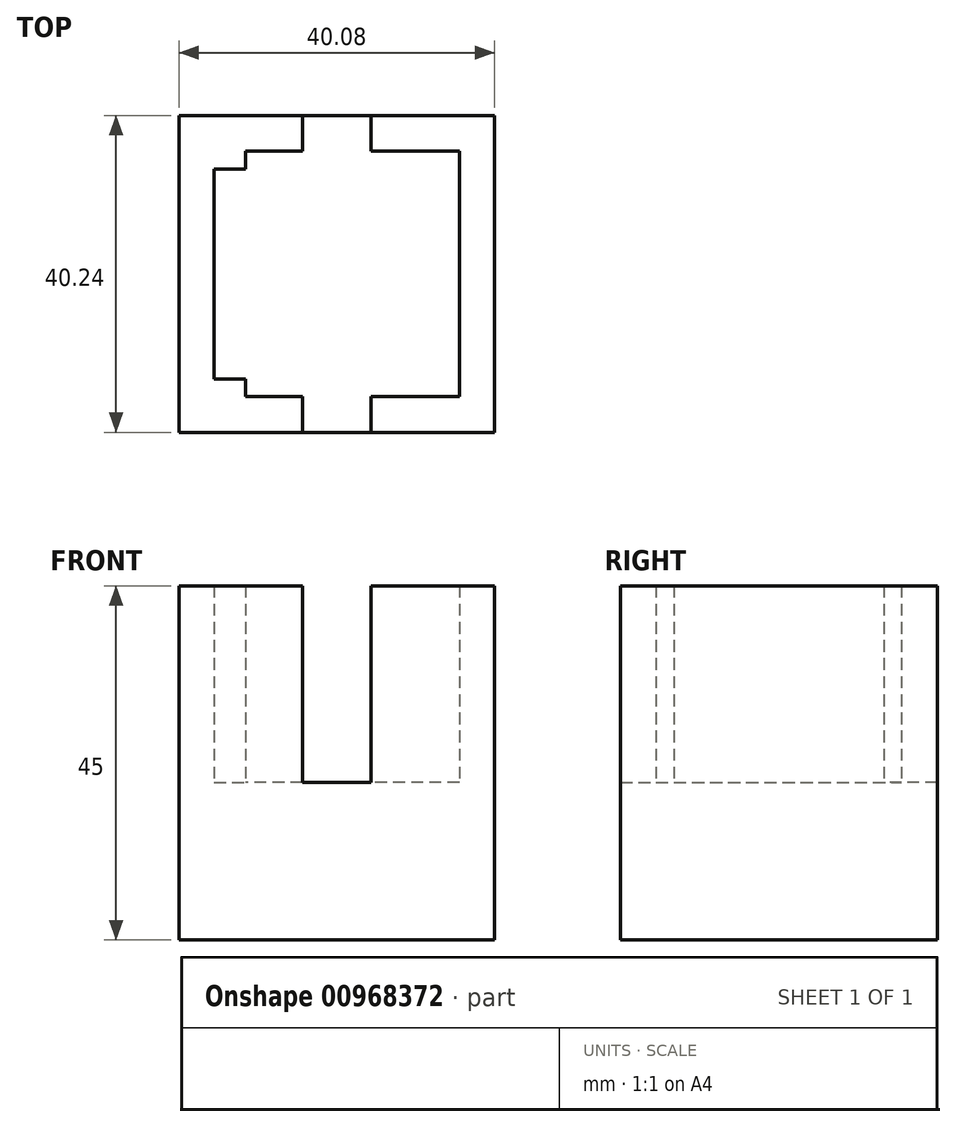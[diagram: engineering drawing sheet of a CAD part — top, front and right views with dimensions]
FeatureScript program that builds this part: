
annotation { "Feature Type Name" : "Feature", "Feature Type Description" : "" }
export const myFeature = defineFeature(function(context is Context, id is Id, definition is map)
    precondition{}
    {
        {
            var Q0;
            Q0=qCreatedBy(makeId("Top.planeOp"),FACE);
            var sketch = newSketch(context, id + "F0", { "sketchPlane" : qUnion([Q0])});
            skLineSegment(sketch, "E0.bottom", {"start": v(40.07, 40.24) * mm, "end": v(0, 40.24) * mm});
            skLineSegment(sketch, "E0.top", {"start": v(40.08, 0) * mm, "end": v(0, 0) * mm});
            skLineSegment(sketch, "E0.left", {"start": v(40.07, 40.24) * mm, "end": v(40.08, 0) * mm});
            skLineSegment(sketch, "E0.right", {"start": v(0, 40.24) * mm, "end": v(0, 0) * mm});
            skSolve(sketch);
        }
        {
            var Q0;
            Q0 = qSketchRegion(id + "F0", true);
            extrude(context, id + "F1", {"entities" : qUnion([Q0]), "depth" : 20 * mm, "offsetDistance" : 25 * mm});
        }
        {
            var Q0;
            Q0=makeQuery(id+"F1.opExtrude","CAP_FACE",FACE,{"disambiguationData":[OSD([sQuery(id+"F0.wireOp",EDGE,"E0.bottom"),sQuery(id+"F0.wireOp",EDGE,"E0.top"),sQuery(id+"F0.wireOp",EDGE,"E0.left"),sQuery(id+"F0.wireOp",EDGE,"E0.right")])],"isStart":false});
            var sketch = newSketch(context, id + "F2", { "sketchPlane" : qUnion([Q0])});
            skLineSegment(sketch, "E1", {"start": v(0, 0) * mm, "end": v(40.07, 40.24) * mm, "construction": true});
            skLineSegment(sketch, "E2.bottom", {"start": v(35.61, 4.54) * mm, "end": v(24.4, 4.54) * mm});
            skLineSegment(sketch, "E2.top", {"start": v(35.61, 35.7) * mm, "end": v(24.4, 35.7) * mm});
            skLineSegment(sketch, "E2.left", {"start": v(35.61, 4.54) * mm, "end": v(35.61, 35.7) * mm});
            skLineSegment(sketch, "E2.right", {"start": v(4.46, 6.77) * mm, "end": v(4.46, 33.46) * mm});
            skPoint(sketch, "E2.middle", {"position": v(20.04, 20.12) * mm});
            skLineSegment(sketch, "E3.bottom", {"start": v(40.08, 0) * mm, "end": v(24.4, 0) * mm});
            skLineSegment(sketch, "E3.top", {"start": v(40.08, 40.24) * mm, "end": v(24.4, 40.24) * mm});
            skLineSegment(sketch, "E3.left", {"start": v(40.08, 0) * mm, "end": v(40.08, 40.24) * mm});
            skLineSegment(sketch, "E3.right", {"start": v(0, 0) * mm, "end": v(0, 40.24) * mm});
            skLineSegment(sketch, "E4.left", {"start": v(24.4, 40.24) * mm, "end": v(24.4, 35.7) * mm});
            skLineSegment(sketch, "E4.right", {"start": v(15.68, 40.24) * mm, "end": v(15.68, 35.7) * mm});
            skPoint(sketch, "E4.middle", {"position": v(20.04, 35.7) * mm});
            skPoint(sketch, "E5.orphan", {"position": v(15.68, 43.35) * mm});
            skPoint(sketch, "E6.orphan", {"position": v(24.4, 43.35) * mm});
            skLineSegment(sketch, "E7.trimOffspring", {"start": v(15.68, 35.7) * mm, "end": v(8.46, 35.7) * mm});
            skLineSegment(sketch, "E8.trimOffspring", {"start": v(15.68, 40.24) * mm, "end": v(0, 40.24) * mm});
            skPoint(sketch, "E4.top.end.orphan", {"position": v(15.68, 28.05) * mm});
            skPoint(sketch, "E4.top.start.orphan", {"position": v(24.4, 28.05) * mm});
            skLineSegment(sketch, "E9", {"start": v(0, 20.12) * mm, "end": v(43.29, 20.12) * mm, "construction": true});
            skPoint(sketch, "E9.endSnap0", {"position": v(40.08, 20.12) * mm});
            skLineSegment(sketch, "E10.MirrorCS", {"start": v(15.68, 0) * mm, "end": v(15.68, 4.54) * mm});
            skLineSegment(sketch, "E11.MirrorCS", {"start": v(24.4, 0) * mm, "end": v(24.4, 4.54) * mm});
            skLineSegment(sketch, "E12.trimOffspring", {"start": v(15.68, 4.54) * mm, "end": v(8.46, 4.54) * mm});
            skLineSegment(sketch, "E13.trimOffspring", {"start": v(15.68, 0) * mm, "end": v(0, 0) * mm});
            skLineSegment(sketch, "E14.top", {"start": v(4.46, 33.46) * mm, "end": v(8.46, 33.46) * mm});
            skLineSegment(sketch, "E14.right", {"start": v(8.46, 35.7) * mm, "end": v(8.46, 33.46) * mm});
            skPoint(sketch, "E14.left.start.orphan", {"position": v(4.46, 35.7) * mm});
            skLineSegment(sketch, "E15.MirrorCS", {"start": v(8.46, 4.54) * mm, "end": v(8.46, 6.77) * mm});
            skLineSegment(sketch, "E16.MirrorCS", {"start": v(4.46, 6.77) * mm, "end": v(8.46, 6.77) * mm});
            skLineSegment(sketch, "E17.trimOffspring", {"start": v(4.52, 4.54) * mm, "end": v(4.46, 4.54) * mm});
            skSolve(sketch);
        }
        {
            var Q0;
            Q0=makeQuery(id+"F2.imprint","IMPRINT",FACE,{"disambiguationData":[TD([[makeQuery(id+"F2.imprint","IMPRINT",EDGE,{"derivedFrom":sQuery(id+"F2.wireOp",EDGE,"E2.right")}),1.0]])]});
            var Q1;
            Q1=makeQuery(id+"F2.imprint","IMPRINT",FACE,{"disambiguationData":[TD([[makeQuery(id+"F2.imprint","IMPRINT",EDGE,{"derivedFrom":sQuery(id+"F2.wireOp",EDGE,"E2.bottom")}),1.0]])]});
            extrude(context, id + "F3", {"entities" : qUnion([Q0, Q1]), "operationType" : NewBodyOperationType.ADD, "depth" : 25 * mm, "offsetDistance" : 25 * mm});
        }
    });
